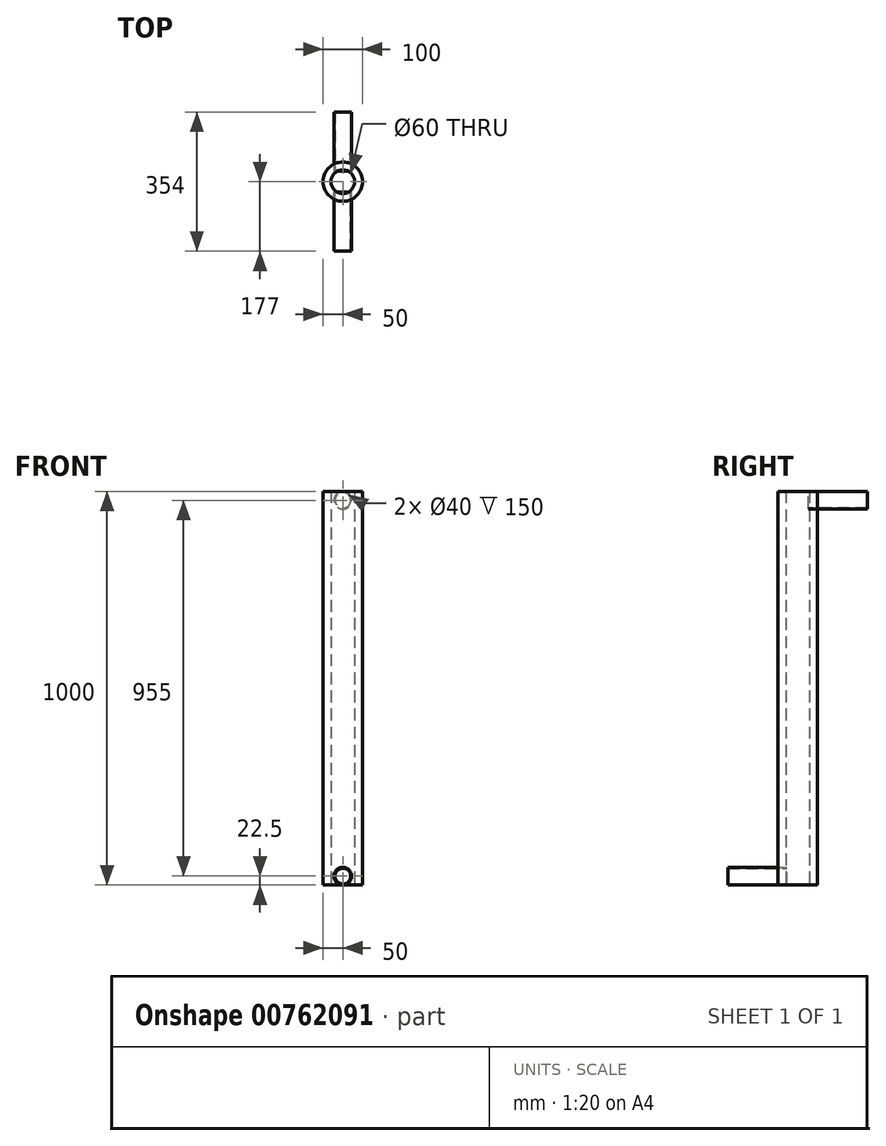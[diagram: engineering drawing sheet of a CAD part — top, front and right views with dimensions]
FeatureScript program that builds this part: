
annotation { "Feature Type Name" : "Feature", "Feature Type Description" : "" }
export const myFeature = defineFeature(function(context is Context, id is Id, definition is map)
    precondition{}
    {
        {
            var Q0;
            Q0=qCreatedBy(makeId("Top.planeOp"),FACE);
            var sketch = newSketch(context, id + "F0", { "sketchPlane" : qUnion([Q0])});
            skCircle(sketch, "E0", {"center": v(0, 0) * mm, "radius": 30 * mm});
            skCircle(sketch, "E1", {"center": v(0, 0) * mm, "radius": 50 * mm});
            skSolve(sketch);
        }
        {
            var Q0;
            Q0=makeQuery(id+"F0.imprint","IMPRINT",FACE,{"disambiguationData":[TD([[makeQuery(id+"F0.imprint","IMPRINT",EDGE,{"derivedFrom":sQuery(id+"F0.wireOp",EDGE,"E0")}),-1.0]])]});
            extrude(context, id + "F1", {"entities" : qUnion([Q0]), "depth" : 1000 * mm, "offsetDistance" : 25 * mm});
        }
        {
            var Q0;
            Q0=qCreatedBy(makeId("Front.planeOp"),FACE);
            var sketch = newSketch(context, id + "F2", { "sketchPlane" : qUnion([Q0])});
            skCircle(sketch, "E2", {"center": v(0, 0) * mm, "radius": 20 * mm});
            skCircle(sketch, "E3", {"center": v(0, 0) * mm, "radius": 22.5 * mm});
            skSolve(sketch);
        }
        {
            var Q0;
            Q0=makeQuery(id+"F2.imprint","IMPRINT",FACE,{"disambiguationData":[TD([[makeQuery(id+"F2.imprint","IMPRINT",EDGE,{"derivedFrom":sQuery(id+"F2.wireOp",EDGE,"E2")}),-1.0]])]});
            extrude(context, id + "F3", {"entities" : qUnion([Q0]), "depth" : 150 * mm, "offsetDistance" : 25 * mm});
        }
        {
            var Q0;
            Q0=makeQuery(id+"F3.opExtrude","SWEPT_BODY",BODY,{"disambiguationData":[OSD([sQuery(id+"F2.wireOp",EDGE,"E2"),sQuery(id+"F2.wireOp",EDGE,"E3")])]});
            transform(context, id + "F4", {"entities" : qUnion([Q0]), "transformType" : TransformType.TRANSLATION_3D, "dx" : 0 * mm, "dy" : -27 * mm, "dz" : 22.5 * mm, "makeCopy" : false});
        }
        {
            var Q0;
            Q0=makeQuery(id+"F3.opExtrude","SWEPT_BODY",BODY,{"disambiguationData":[OSD([sQuery(id+"F2.wireOp",EDGE,"E2"),sQuery(id+"F2.wireOp",EDGE,"E3")])]});
            var Q1;
            Q1=qCreatedBy(makeId("Front.planeOp"),FACE);
            mirror(context, id + "F5", {"entities" : qUnion([Q0]), "mirrorPlane" : qUnion([Q1])});
        }
        {
            var Q0;
            Q0=makeQuery(id+"F5.opPattern","COPY",BODY,{"derivedFrom":makeQuery(id+"F3.opExtrude","SWEPT_BODY",BODY,{"disambiguationData":[OSD([sQuery(id+"F2.wireOp",EDGE,"E2"),sQuery(id+"F2.wireOp",EDGE,"E3")])]}),"instanceName":"1"});
            transform(context, id + "F6", {"entities" : qUnion([Q0]), "transformType" : TransformType.TRANSLATION_3D, "dx" : 0 * mm, "dy" : 0 * mm, "dz" : 955 * mm, "makeCopy" : false});
        }
    });
